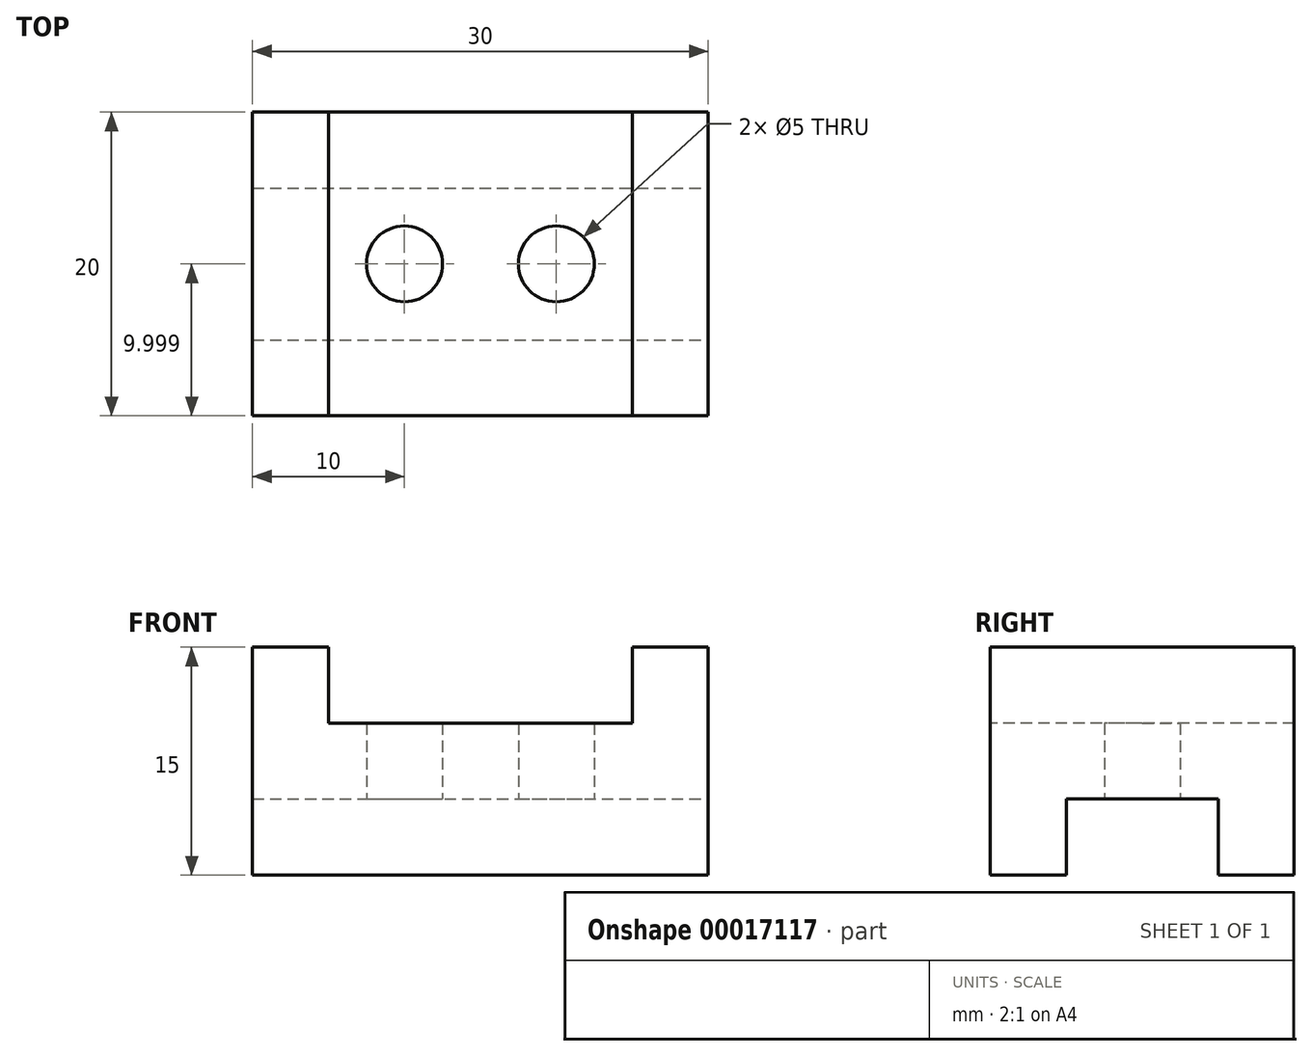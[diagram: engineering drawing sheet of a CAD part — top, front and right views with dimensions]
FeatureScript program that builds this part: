
annotation { "Feature Type Name" : "Feature", "Feature Type Description" : "" }
export const myFeature = defineFeature(function(context is Context, id is Id, definition is map)
    precondition{}
    {
        {
            var Q0;
            Q0=qCreatedBy(makeId("Top.planeOp"),FACE);
            var sketch = newSketch(context, id + "F0", { "sketchPlane" : qUnion([Q0])});
            skLineSegment(sketch, "E0.bottom", {"start": v(-11.06, 10.86) * mm, "end": v(18.94, 10.86) * mm});
            skLineSegment(sketch, "E0.top", {"start": v(-11.06, -9.14) * mm, "end": v(18.94, -9.14) * mm});
            skLineSegment(sketch, "E0.left", {"start": v(-11.06, 10.86) * mm, "end": v(-11.06, -9.14) * mm});
            skLineSegment(sketch, "E0.right", {"start": v(18.94, 10.86) * mm, "end": v(18.94, -9.14) * mm});
            skLineSegment(sketch, "E1", {"start": v(-6.06, 10.86) * mm, "end": v(-6.06, -9.14) * mm});
            skLineSegment(sketch, "E2", {"start": v(13.94, 10.86) * mm, "end": v(13.94, -9.14) * mm});
            skCircle(sketch, "E3", {"center": v(-1.06, 0.86) * mm, "radius": 2.5 * mm});
            skCircle(sketch, "E4", {"center": v(8.94, 0.86) * mm, "radius": 2.5 * mm});
            skSolve(sketch);
        }
        {
            var Q0;
            {var subQ1=sQuery(id+"F0.wireOp",EDGE,"E1");Q0=makeQuery(id+"F0.imprint","IMPRINT",FACE,{"disambiguationData":[TD([[makeQuery(id+"F0.imprint","IMPRINT",EDGE,{"derivedFrom":subQ1}),1.0]])]});}
            extrude(context, id + "F1", {"entities" : qUnion([Q0]), "depth" : 10 * mm});
        }
        {
            var Q0;
            {var subQ1=sQuery(id+"F0.wireOp",EDGE,"E0.left");Q0=makeQuery(id+"F0.imprint","IMPRINT",FACE,{"disambiguationData":[TD([[makeQuery(id+"F0.imprint","IMPRINT",EDGE,{"derivedFrom":subQ1}),1.0]])]});}
            var Q1;
            {var subQ1=sQuery(id+"F0.wireOp",EDGE,"E0.right");Q1=makeQuery(id+"F0.imprint","IMPRINT",FACE,{"disambiguationData":[TD([[makeQuery(id+"F0.imprint","IMPRINT",EDGE,{"derivedFrom":subQ1}),-1.0]])]});}
            extrude(context, id + "F2", {"entities" : qUnion([Q0, Q1]), "operationType" : NewBodyOperationType.ADD, "depth" : 15 * mm});
        }
        {
            var Q0;
            Q0=makeQuery(id+"F2.opExtrude","SWEPT_FACE",FACE,{"disambiguationData":[OSD([sQuery(id+"F0.wireOp",EDGE,"E0.right")])]});
            var sketch = newSketch(context, id + "F3", { "sketchPlane" : qUnion([Q0])});
            skLineSegment(sketch, "E5", {"start": v(-4.14, 0) * mm, "end": v(-4.14, 5) * mm});
            skLineSegment(sketch, "E6", {"start": v(-4.14, 5) * mm, "end": v(5.86, 5) * mm});
            skLineSegment(sketch, "E7", {"start": v(5.86, 5) * mm, "end": v(5.86, 0) * mm});
            skSolve(sketch);
        }
        {
            var Q0;
            {var subQ2=sQuery(id+"F3.wireOp",EDGE,"E5");Q0=makeQuery(id+"F3.imprint","IMPRINT",FACE,{"disambiguationData":[TD([[makeQuery(id+"F3.imprint","IMPRINT",EDGE,{"derivedFrom":subQ2}),-1.0]])]});}
            extrude(context, id + "F4", {"entities" : qUnion([Q0]), "operationType" : NewBodyOperationType.REMOVE, "endBound" : BoundingType.THROUGH_ALL, "oppositeDirection" : true, "depth" : 25 * mm});
        }
    });
